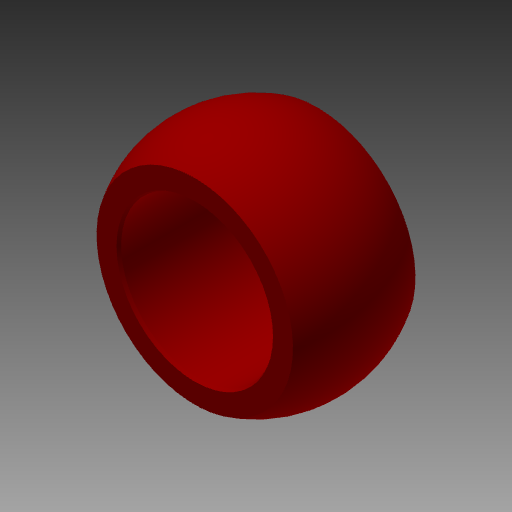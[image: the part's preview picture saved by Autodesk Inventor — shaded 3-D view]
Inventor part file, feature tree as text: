
AUTODESK INVENTOR PART (.ipt)
format: ipt  version: 2017.1 (Build 211199000, 199)  size: 136,192 bytes
history: native  units: mm (DEFAULTED — no unit token found)
features: sketch x2, revolve x1, extrude x1, hole x1, chamfer x1
ambient origin geometry x8: Origin, YZ Plane, XZ Plane, XY Plane, X Axis, Y Axis, Z Axis, Center Point
bodies: Solid1 (feature_tree)
feature tree (6):
  revolve  "Revolution1"  Angle=90.0deg
  extrude  "Extrusion3"  Depth=6.35mm TaperAngle=0.0deg
  hole  "Hole1"  [1 undecoded]
  chamfer  "Chamfer1"  Distance=0.3048mm Angle=30.0deg
  sketch  "Sketch1"  dims[d0=24.003mm d1=90.0deg]
  sketch  "Sketch4"  dims[d8=12.7mm d9=25.4mm d10=0.0mm d11=25.4mm d12=25.4mm d13=15.875mm d14=12.7mm d15=9.525mm d16=6.35mm d17=14.3117mm d18=19.05mm d19=20.594885mm d20=0.3048mm d21=3.175mm d22=30.0deg]
note: 1 required parameter value undecoded (feature->parameter linkage not recoverable at this tier; creation-order binding heuristic only, values carry confidence <= 0.55)
